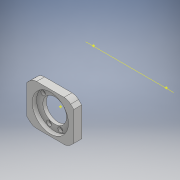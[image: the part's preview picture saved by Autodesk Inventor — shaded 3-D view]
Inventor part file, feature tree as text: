
AUTODESK INVENTOR PART (.ipt)
format: ipt  version: 2018 (Build 220112000, 112)  size: 751,616 bytes
history: native  units: mm
features: sketch x38, projected_geometry x38, extrude x32, other x10, chamfer x7, fillet x5, hole x4, reference x3, mirror x1, plane x1
ambient origin geometry x8: Origin, YZ Plane, XZ Plane, XY Plane, X Axis, Y Axis, Z Axis, Center Point
bodies: Solid1 (feature_tree)
feature tree (139):
  extrude  "Extrusion1"  Depth=45.0mm
  extrude  "Extrusion2"  Depth=2.25mm
  hole  "Hole1"  [1 undecoded]
  hole  "Hole2"  [1 undecoded]
  fillet  "Fillet1"  Radius=14.0mm
  extrude  "Extrusion3"  Depth=18.5mm
  extrude  "Extrusion4"  Depth=10.0mm
  extrude  "Extrusion5"  Depth=2.0mm
  extrude  "Extrusion6"  Depth=2.0mm
  hole  "Hole3"  [1 undecoded]
  extrude  "Extrusion7"  Depth=2.0mm
  extrude  "Extrusion8"  Depth=1.0mm TaperAngle=0.0deg
  extrude  "Extrusion9"  Depth=24.5mm
  extrude  "Extrusion10"  Depth=10.0mm
  extrude  "Extrusion11"  Depth=14.5mm
  extrude  "Extrusion13"  Depth=14.5mm
  extrude  "Extrusion14"  Depth=5.0mm
  extrude  "Extrusion15"  Depth=2.25mm
  extrude  "Extrusion16"  Depth=5.0mm
  extrude  "Extrusion17"  Depth=9.0mm
  chamfer  "Chamfer1"  Distance=1.0mm
  fillet  "Fillet7"  Radius=20.7mm
  fillet  "Fillet8"  Radius=32.0mm
  mirror  "Mirror1"
  sketch  "Sketch26"  dims[d55=2.25mm d56=5.0mm]
  extrude  "Extrusion24"  Depth=1.0mm TaperAngle=0.0deg
  extrude  "Extrusion25"  Depth=8.0mm
  extrude  "Extrusion26"  Depth=0.2mm TaperAngle=0.0deg
  extrude  "Extrusion27"  Depth=5.0mm TaperAngle=0.0deg
  other  "Work Axis1"
  plane  "Work Plane2"
  extrude  "Extrusion28"  Depth=0.2mm TaperAngle=0.0deg
  extrude  "Extrusion29"  Depth=2.0mm TaperAngle=45.0deg
  chamfer  "Chamfer2"  Distance=15.0mm
  extrude  "Extrusion31"  Depth=2.2mm TaperAngle=0.0deg
  chamfer  "Chamfer3"  Distance=15.0mm
  chamfer  "Chamfer4"  Distance=15.0mm
  extrude  "Extrusion32"  Depth=2.2mm
  chamfer  "Chamfer5"  Distance=41.5mm
  extrude  "Extrusion33"  Depth=2.2mm
  sketch  "Sketch41"  dims[d100=0.2mm d101=0.0mm d102=2.5mm d103=2.0mm d104=45.0deg]
  extrude  "Extrusion34"  Depth=2.2mm
  chamfer  "Chamfer6"  Distance=7.0mm
  fillet  "Fillet9"  Radius=100.0mm
  extrude  "Extrusion35"  Depth=2.2mm TaperAngle=0.0deg
  extrude  "Extrusion36"  Depth=2.0mm TaperAngle=45.0deg
  chamfer  "Chamfer7"  [1 undecoded]
  fillet  "Fillet10"  Radius=11.5mm
  extrude  "Extrusion37"  Depth=2.2mm
  extrude  "Extrusion38"  Depth=2.2mm
  extrude  "Extrusion39"  Depth=2.2mm TaperAngle=0.0deg
  extrude  "Extrusion40"  Depth=2.0mm TaperAngle=45.0deg
  hole  "Hole6"  [1 undecoded]
  sketch  "Sketch1"  dims[d0=24.5mm d1=45.0mm]
  sketch  "Sketch2"  dims[d2=1.95mm d3=0.0mm d4=2.25mm]
  projected_geometry  "Projected Loop1"
  sketch  "Sketch3"  dims[d5=20.0mm d6=2.25mm]
  projected_geometry  "Projected Loop2"
  sketch  "Sketch4"  dims[d7=5.25mm d8=5.25mm d9=14.0mm]
  projected_geometry  "Projected Loop3"
  sketch  "Sketch5"  dims[d10=5.25mm d11=18.5mm]
  projected_geometry  "Projected Loop4"
  sketch  "Sketch6"  dims[d12=10.0mm d13=0.0mm d14=20.5mm]
  projected_geometry  "Projected Loop5"
  sketch  "Sketch7"  dims[d15=2.0mm d16=2.195mm]
  projected_geometry  "Projected Loop6"
  sketch  "Sketch8"  dims[d17=2.0mm]
  projected_geometry  "Projected Loop7"
  sketch  "Sketch9"  dims[d18=2.4mm d19=6.0mm d20=4.4mm d21=2.0mm d22=90.0deg d23=8.0mm d24=20.594885mm d25=20.5mm]
  projected_geometry  "Projected Loop8"
  projected_geometry  "Projected Loop9"
  sketch  "Sketch10"  dims[d26=26.65mm d27=2.0mm]
  projected_geometry  "Projected Loop10"
  projected_geometry  "Projected Loop11"
  sketch  "Sketch11"  dims[d28=2.0mm]
  projected_geometry  "Projected Loop12"
  sketch  "Sketch12"  dims[d29=2.4mm d30=6.0mm d31=4.4mm d32=2.0mm d33=90.0deg d34=8.0mm d35=20.594885mm d36=0.5mm]
  sketch  "Sketch13"  dims[d37=18.0mm d38=1.0mm d39=0.0mm]
  sketch  "Sketch14"  dims[d41=5.0mm d42=0.0mm d43=24.5mm]
  projected_geometry  "Projected Loop13"
  sketch  "Sketch16"  dims[d44=1.15mm d45=0.0mm d46=10.0mm]
  projected_geometry  "Projected Loop14"
  sketch  "Sketch17"  dims[d47=21.0mm d48=14.5mm]
  projected_geometry  "Projected Loop15"
  sketch  "Sketch18"  dims[d49=20.0mm d50=14.5mm]
  projected_geometry  "Projected Loop16"
  sketch  "Sketch19"  dims[d51=24.5mm d52=5.0mm]
  projected_geometry  "Projected Loop17"
  sketch  "Sketch20"  dims[d53=5.0mm d54=2.25mm]
  projected_geometry  "Projected Loop18"
  projected_geometry  "Projected Loop25"
  sketch  "Sketch31"  dims[d57=5.0mm d58=9.0mm]
  projected_geometry  "Projected Loop30"
  reference  "Reference1"
  sketch  "Sketch32"  dims[d59=14.75mm]
  projected_geometry  "Projected Loop31"
  sketch  "Sketch33"  dims[d60=4.0mm d61=1.0mm d62=0.0mm d63=20.7mm]
  projected_geometry  "Projected Loop32"
  sketch  "Sketch34"  dims[d64=2.4mm d65=6.0mm d66=4.4mm d67=2.0mm d68=90.0deg d69=8.0mm d70=20.594885mm d72=32.0mm]
  projected_geometry  "Projected Loop33"
  other  "Work Point1"
  other  "Work Point2"
  other  "Work Point3"
  sketch  "Sketch35"  dims[d73=3.0mm d74=0.0mm d75=1.0mm d76=0.0mm]
  sketch  "Sketch37"  dims[d77=12.25mm d78=0.0mm d80=8.0mm]
  projected_geometry  "Projected Loop34"
  sketch  "Sketch38"  dims[d81=4.5mm d82=0.0mm d84=0.2mm d85=0.0mm]
  sketch  "Sketch39"  dims[d91=8.0mm d92=0.0mm d93=5.0mm d94=0.0mm]
  sketch  "Sketch40"  dims[d95=5.0mm d96=0.0mm d98=0.2mm d99=0.0mm]
  projected_geometry  "Projected Loop35"
  projected_geometry  "Projected Loop36"
  projected_geometry  "Projected Loop37"
  projected_geometry  "Projected Loop38"
  sketch  "Sketch42"  dims[d105=1.5mm]
  projected_geometry  "Projected Loop39"
  sketch  "Sketch43"  dims[d114=0.5mm]
  reference  "Reference2"
  reference  "Reference3"
  sketch  "Sketch45"  dims[d130=60.0mm]
  projected_geometry  "Projected Loop40"
  sketch  "Sketch46"  dims[d131=36.0mm]
  projected_geometry  "Projected Loop41"
  sketch  "Sketch48"  dims[d146=40.0mm]
  projected_geometry  "Projected Loop43"
  sketch  "Sketch49"  dims[d147=60.0mm]
  projected_geometry  "Projected Loop44"
  projected_geometry  "Projected Loop45"
  sketch  "Sketch50"  dims[d148=0.0mm]
  projected_geometry  "Projected Loop46"
  sketch  "Sketch52"  dims[d149=2.3mm d150=15.0mm d151=0.0mm d152=15.0mm d153=0.0mm d154=15.0mm d155=0.0mm d156=15.0mm d157=0.0mm d158=20.5mm d159=41.5mm d160=14.0mm d161=14.0mm d162=7.0mm d165=100.0mm d166=0.0mm d167=100.0mm d168=0.0mm d169=6.0mm d170=2.0mm d171=45.0deg d172=0.0mm d173=11.5mm d175=11.5mm d176=11.5mm d179=100.0mm d180=0.0mm d181=5.0mm d182=2.0mm d183=45.0deg d184=5.0mm d185=2.0mm d186=45.0deg d187=8.0mm d188=100.0mm d189=0.0mm d190=5.0mm d191=2.0mm d192=45.0deg d193=100.0mm d194=0.0mm d195=100.0mm d196=0.0mm d197=5.0mm d198=2.0mm d199=45.0deg d200=8.0mm d202=15.0deg d204=10.970628mm d205=15.470628mm d206=2.5mm d207=0.0mm d208=2.5mm d209=0.0mm d210=3.0mm d211=2.0mm d212=45.0deg d213=2.0mm d215=15.0deg d216=4.0mm d217=4.0mm d218=5.0mm d219=0.0mm d222=32.07mm d223=3.9mm d224=0.0mm d225=2.8mm d226=0.0mm d227=7.0mm d228=0.0mm d229=5.0mm d230=2.2mm d231=6.0mm d232=4.4mm d233=2.2mm d234=90.0deg d235=8.0mm d236=20.594885mm]
  projected_geometry  "Projected Loop47"
  parser-record x1  (decoder bookkeeping rows leaked as tree rows — omitted from the tree; the rows remain in map.json)
  other  "servocheck.iam"
  other  "LX-16A:3"
  other  "DUOPAN-SG-SJ_10"
  projected_geometry  "Project Cut Edges1"
  projected_geometry  "Project Cut Edges3"
  other  "bottomarm:1"
  other  "arm1:1"
note: 5 required parameter values undecoded (feature->parameter linkage not recoverable at this tier; creation-order binding heuristic only, values carry confidence <= 0.55)
note: 1 file-system path scrubbed to <path> (originals preserved in map.json)
